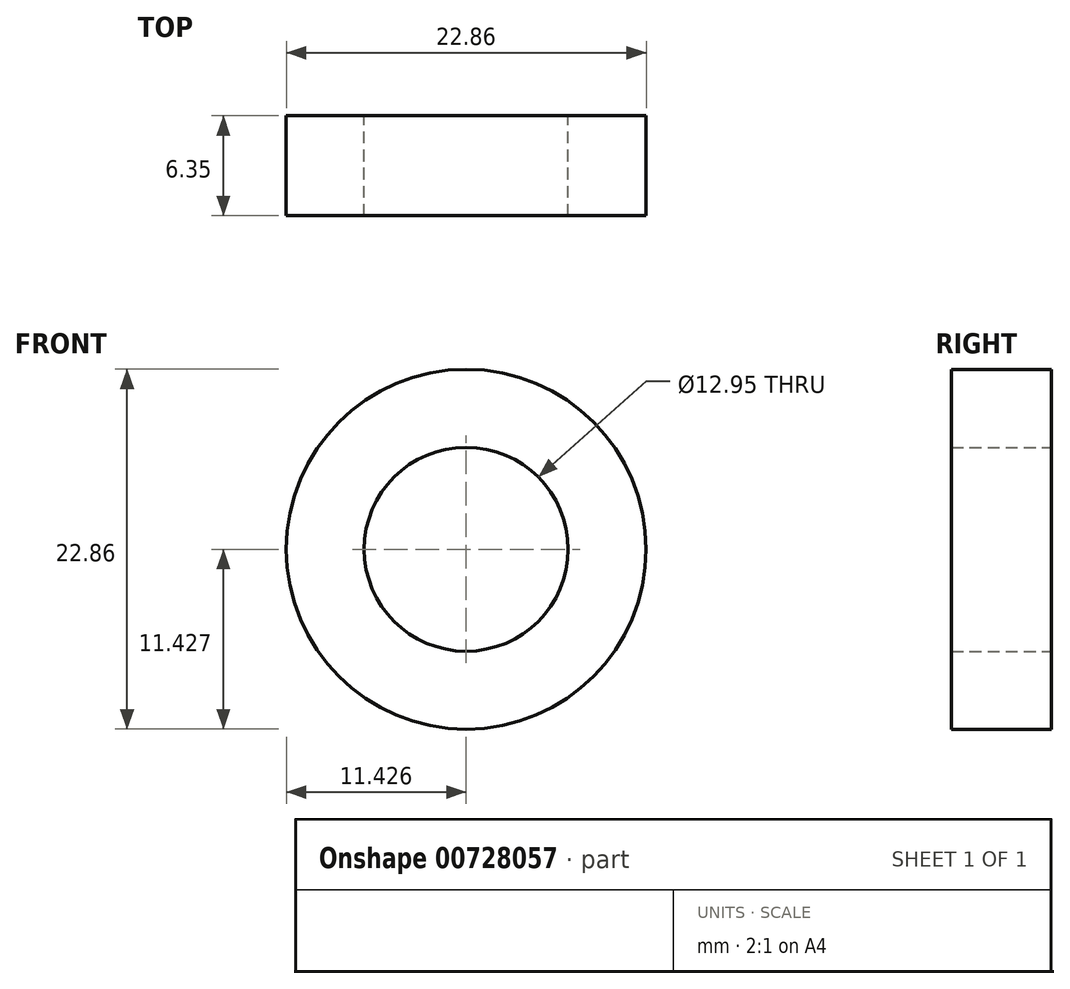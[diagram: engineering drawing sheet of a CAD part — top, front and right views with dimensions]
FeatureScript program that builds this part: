
annotation { "Feature Type Name" : "Feature", "Feature Type Description" : "" }
export const myFeature = defineFeature(function(context is Context, id is Id, definition is map)
    precondition{}
    {
        {
            var Q0;
            Q0=qCreatedBy(makeId("Front.planeOp"),FACE);
            var sketch = newSketch(context, id + "F0", { "sketchPlane" : qUnion([Q0])});
            skCircle(sketch, "E0", {"center": v(26.53, 16.27) * mm, "radius": 6.48 * mm});
            skCircle(sketch, "E1", {"center": v(26.53, 16.27) * mm, "radius": 11.43 * mm});
            skSolve(sketch);
        }
        {
            var Q0;
            Q0=makeQuery(id+"F0.imprint","IMPRINT",FACE,{"disambiguationData":[TD([[makeQuery(id+"F0.imprint","IMPRINT",EDGE,{"derivedFrom":sQuery(id+"F0.wireOp",EDGE,"E0")}),-1.0]])]});
            extrude(context, id + "F1", {"entities" : qUnion([Q0]), "depth" : 6.35 * mm, "offsetDistance" : 25.4 * mm});
        }
    });
